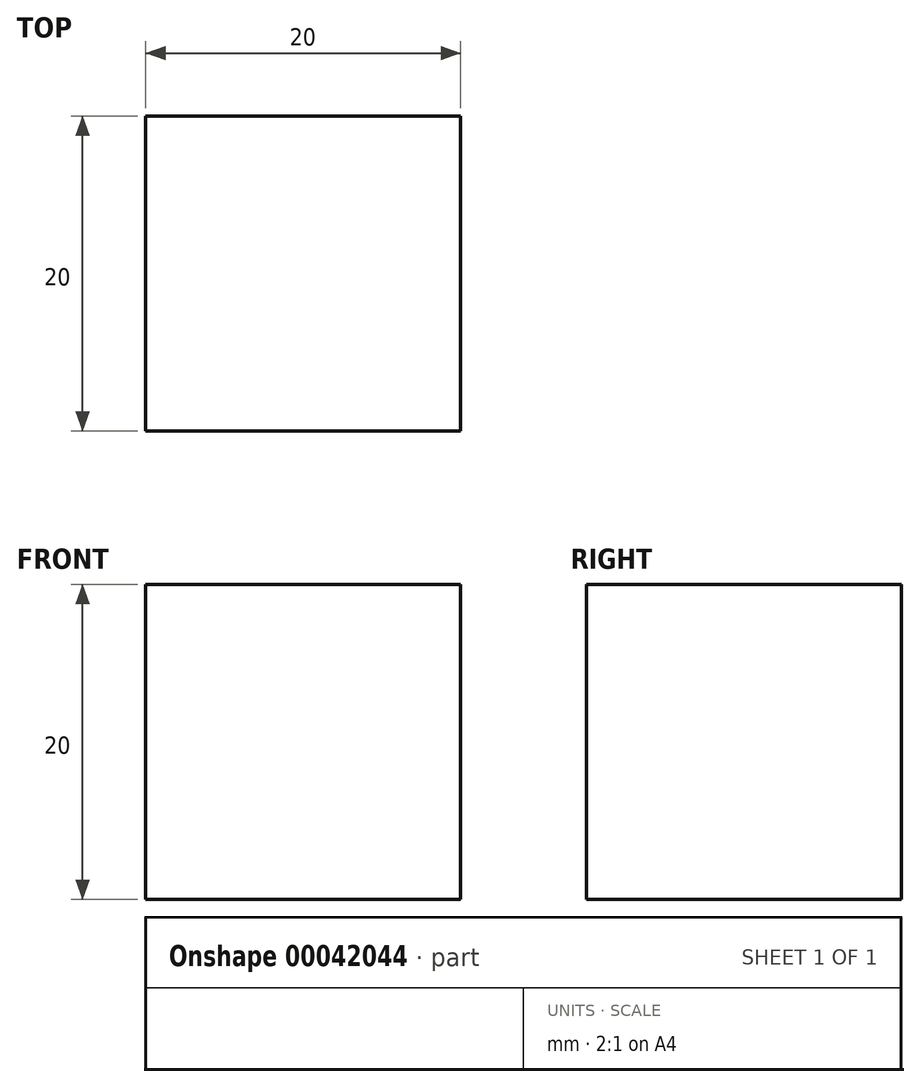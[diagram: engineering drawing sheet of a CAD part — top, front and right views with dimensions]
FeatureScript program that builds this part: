
annotation { "Feature Type Name" : "Feature", "Feature Type Description" : "" }
export const myFeature = defineFeature(function(context is Context, id is Id, definition is map)
    precondition{}
    {
        {
            var Q0;
            Q0=qCreatedBy(makeId("Front.planeOp"),FACE);
            var sketch = newSketch(context, id + "F0", { "sketchPlane" : qUnion([Q0])});
            skLineSegment(sketch, "E0.bottom", {"start": v(-10, 10) * mm, "end": v(10, 10) * mm});
            skLineSegment(sketch, "E0.top", {"start": v(-10, -10) * mm, "end": v(10, -10) * mm});
            skLineSegment(sketch, "E0.left", {"start": v(-10, 10) * mm, "end": v(-10, -10) * mm});
            skLineSegment(sketch, "E0.right", {"start": v(10, 10) * mm, "end": v(10, -10) * mm});
            skPoint(sketch, "E1", {"position": v(0, 10) * mm});
            skPoint(sketch, "E2", {"position": v(10, 0) * mm});
            skSolve(sketch);
        }
        {
            var Q0;
            Q0 = qSketchRegion(id + "F0", true);
            extrude(context, id + "F1", {"entities" : qUnion([Q0]), "endBound" : BoundingType.SYMMETRIC, "depth" : 20 * mm});
        }
    });
